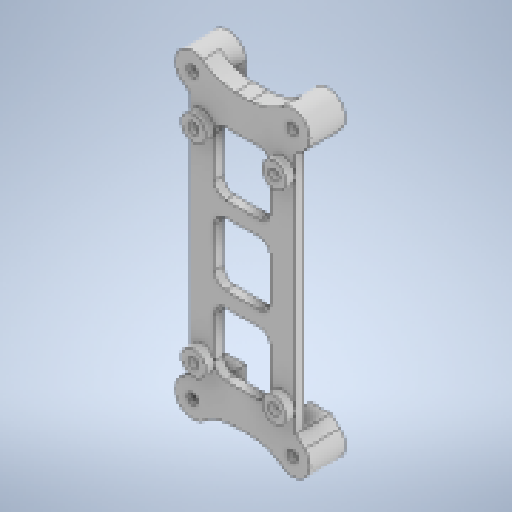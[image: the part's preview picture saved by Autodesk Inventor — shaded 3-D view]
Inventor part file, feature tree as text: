
AUTODESK INVENTOR PART (.ipt)
format: ipt  version: 2023 (Build 270158000, 158)  size: 485,888 bytes
history: native  units: in
note: dims shown in document units (in); Inventor stores cm internally (conversion verified against a paired STEP export)
features: reference x8, extrude x5, sketch x5, other x3, projected_geometry x1
ambient origin geometry x8: Origin, YZ Plane, XZ Plane, XY Plane, X Axis, Y Axis, Z Axis, Center Point
bodies: Solid1 (feature_tree)
feature tree (22):
  extrude  "Extrusion1"  Depth=0.2756in
  extrude  "Extrusion2"  Depth=0.1772in
  extrude  "Extrusion3"  Depth=0.125in
  extrude  "Extrusion4"  Depth=0.25in TaperAngle=0.0deg
  extrude  "Extrusion6"  Depth=0.125in
  sketch  "Sketch1"  dims[d0=0.2756in d1=0.2756in]
  reference  "Reference1"
  reference  "Reference2"
  sketch  "Sketch2"  dims[d2=2.9in d5=0.1772in]
  sketch  "Sketch3"  dims[d6=0.1772in d9=0.125in]
  sketch  "Sketch4"  dims[d10=0.125in d11=0.25in d12=0.0in]
  projected_geometry  "Projected Loop1"
  sketch  "Sketch6"  dims[d13=0.2756in d14=2.2835in d15=0.9055in d16=1.1811in d17=0.5906in d18=0.2756in d19=0.2756in d20=0.2756in d22=0.9055in d23=2.2835in d24=0.4528in d27=0.4854in d29=0.4854in d30=0.1in d31=0.0in d32=0.7087in d33=0.7087in d34=0.7087in d35=0.1705in d36=0.1705in d37=0.125in d38=0.1181in d39=0.1181in d40=0.1181in d41=0.1181in d42=0.1in d43=0.0in d44=0.15in d45=0.0in d50=0.125in d51=0.0in d52=0.5in d53=0.0344in]
  reference  "Reference3"
  reference  "Reference4"
  reference  "Reference5"
  reference  "Reference6"
  reference  "Reference7"
  reference  "Reference8"
  other  "<userpath>\OneDrive - purdue.edu\Senior_Year\Fall_2022\ECE47700\mechanical\ECE477.iam"
  other  "ECE477.iam"
  other  "Source Two v0.1_import:1"
